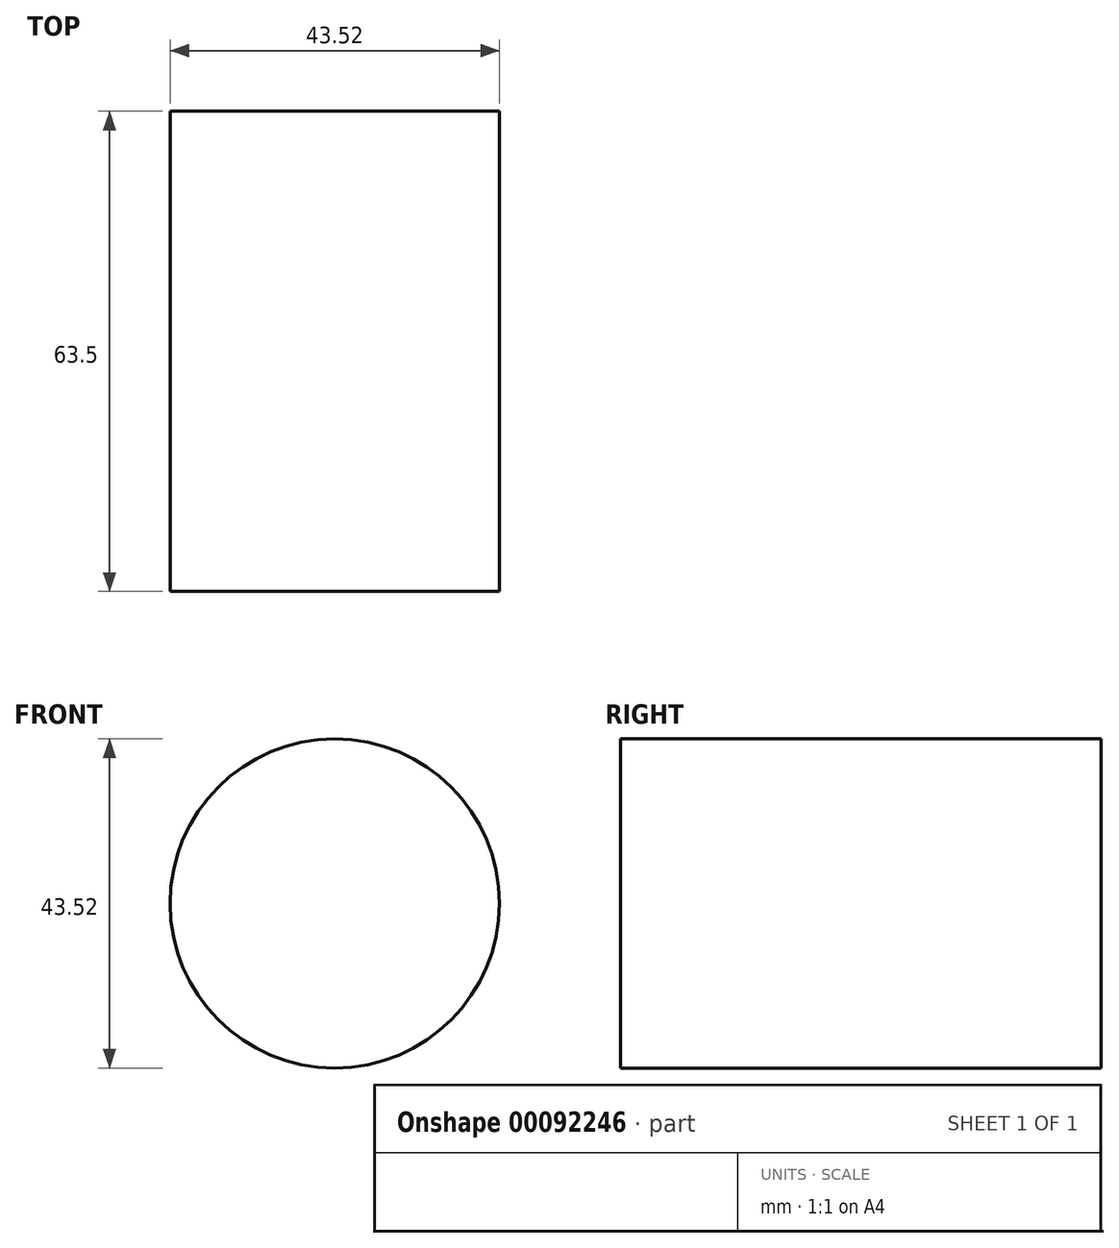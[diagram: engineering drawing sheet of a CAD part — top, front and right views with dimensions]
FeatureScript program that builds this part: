
annotation { "Feature Type Name" : "Feature", "Feature Type Description" : "" }
export const myFeature = defineFeature(function(context is Context, id is Id, definition is map)
    precondition{}
    {
        {
            var Q0;
            Q0=qCreatedBy(makeId("Front.planeOp"),FACE);
            var sketch = newSketch(context, id + "F0", { "sketchPlane" : qUnion([Q0])});
            skCircle(sketch, "E0", {"center": v(-41.94, 62.7) * mm, "radius": 21.76 * mm});
            skSolve(sketch);
        }
        {
            var Q0;
            Q0=sQuery(id+"F0.wireOp",EDGE,"E0");
            extrude(context, id + "F1", {"bodyType" : ToolBodyType.SURFACE, "surfaceEntities" : qUnion([Q0]), "depth" : 63.5 * mm});
        }
    });
